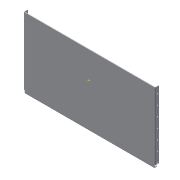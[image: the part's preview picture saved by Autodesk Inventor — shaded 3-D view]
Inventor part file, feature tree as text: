
AUTODESK INVENTOR PART (.ipt)
format: ipt  version: 2016 SP2 (Build 200236200, 236)  size: 149,504 bytes
history: native  units: mm
features: sketch x2, extrude x1
ambient origin geometry x8: Origin, YZ Plane, XZ Plane, XY Plane, X Axis, Y Axis, Z Axis, Center Point
bodies: Solid1 (feature_tree)
feature tree (3):
  sketch  "Sketch1"  dims[d0=54.5mm d1=0.0mm]
  extrude  "Extrusion1"  [1 undecoded]
  sketch  "Sketch2"
note: 1 required parameter value undecoded (feature->parameter linkage not recoverable at this tier; creation-order binding heuristic only, values carry confidence <= 0.55)
